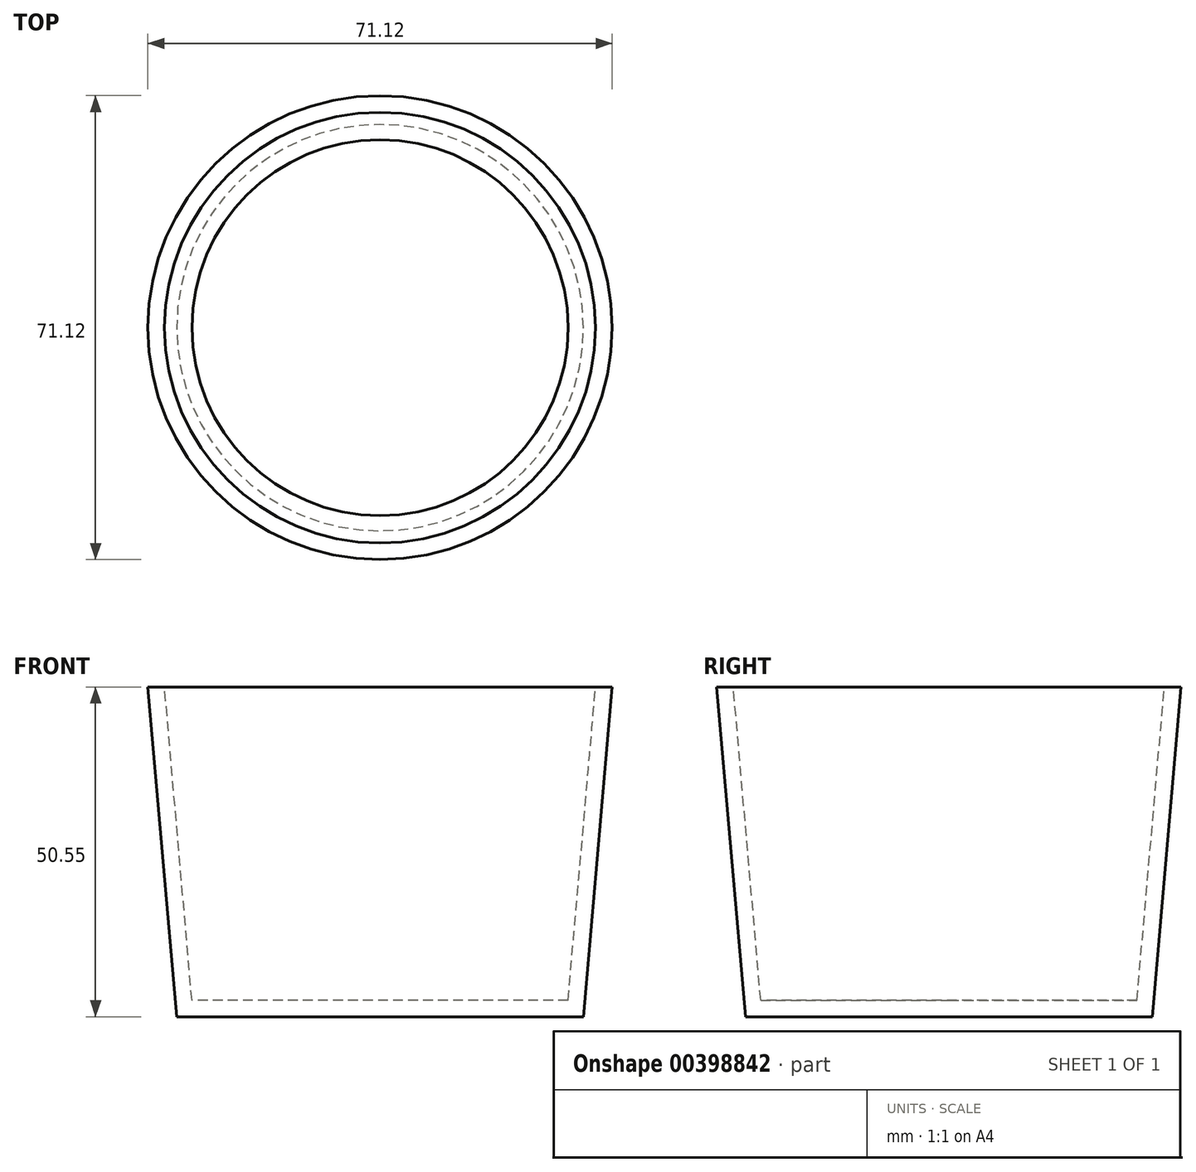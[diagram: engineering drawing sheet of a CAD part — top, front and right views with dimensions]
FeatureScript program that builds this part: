
annotation { "Feature Type Name" : "Feature", "Feature Type Description" : "" }
export const myFeature = defineFeature(function(context is Context, id is Id, definition is map)
    precondition{}
    {
        {
            var Q0;
            Q0=qCreatedBy(makeId("Top.planeOp"),FACE);
            var sketch = newSketch(context, id + "F0", { "sketchPlane" : qUnion([Q0])});
            skCircle(sketch, "E0", {"center": v(0, 0) * mm, "radius": 31.14 * mm});
            skSolve(sketch);
        }
        {
            var Q0;
            Q0=makeQuery(id+"F0.imprint","IMPRINT",FACE,{"disambiguationData":[TD([[makeQuery(id+"F0.imprint","IMPRINT",EDGE,{"derivedFrom":sQuery(id+"F0.wireOp",EDGE,"E0")}),1.0]])]});
            extrude(context, id + "F1", {"entities" : qUnion([Q0]), "depth" : 50.55 * mm, "hasDraft" : true, "draftAngle" : 5 * degree});
        }
        {
            var Q0;
            Q0=makeQuery(id+"F1.opExtrude","CAP_FACE",FACE,{"disambiguationData":[OSD([sQuery(id+"F0.wireOp",EDGE,"E0")])],"isStart":false});
            shell(context, id + "F2", {"entities" : qUnion([Q0]), "thickness" : 2.54 * mm});
        }
    });
